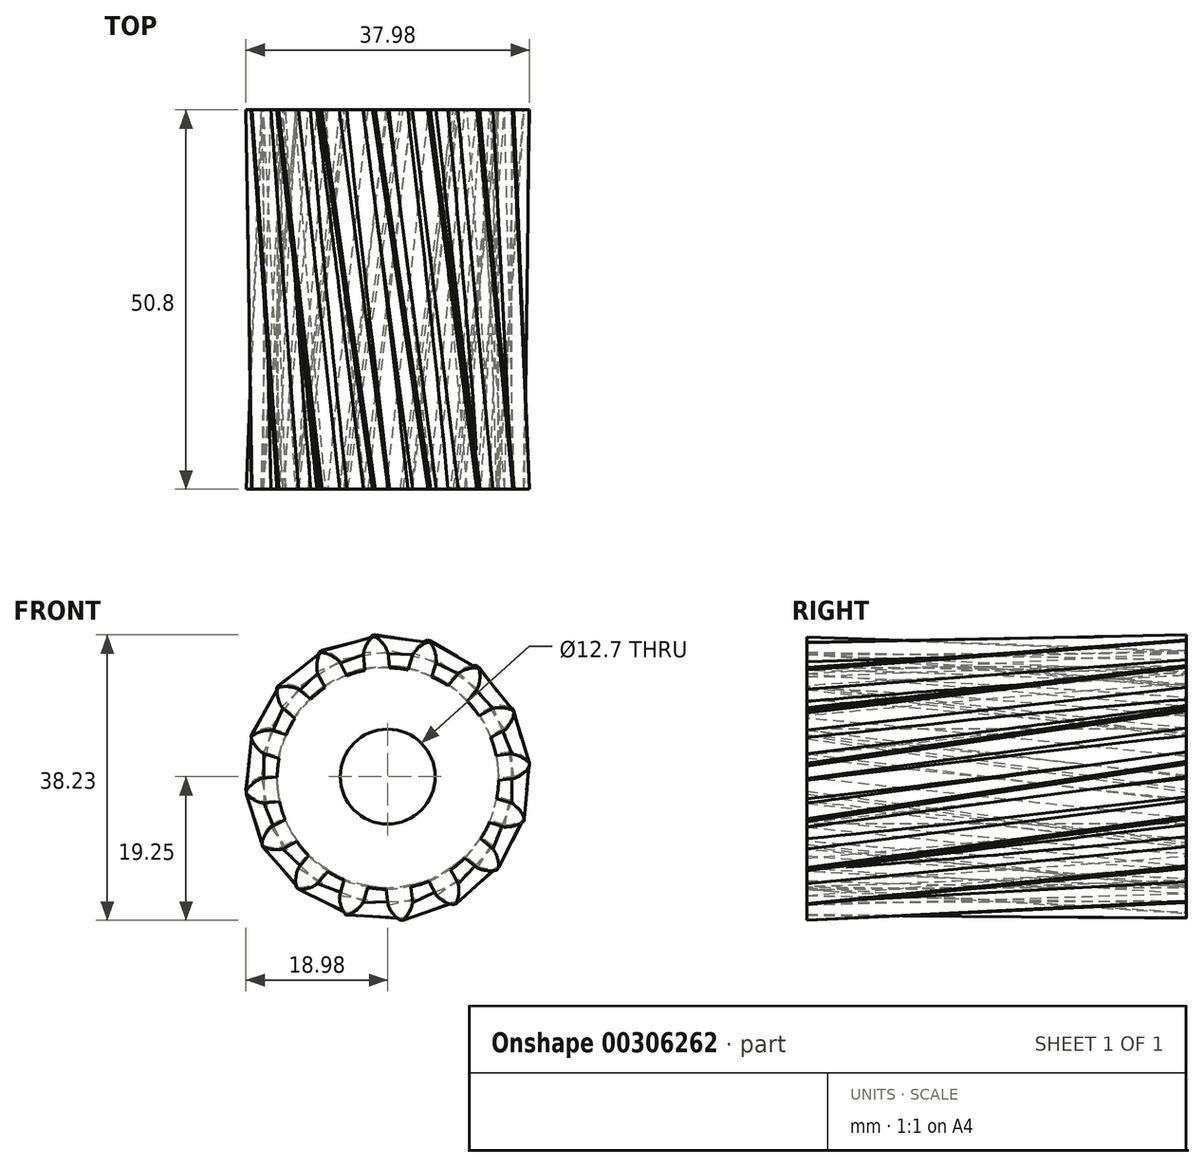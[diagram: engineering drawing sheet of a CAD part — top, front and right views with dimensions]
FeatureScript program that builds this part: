
annotation { "Feature Type Name" : "Feature", "Feature Type Description" : "" }
export const myFeature = defineFeature(function(context is Context, id is Id, definition is map)
    precondition{}
    {
        {
            var Q0;
            Q0=qCreatedBy(makeId("Front.planeOp"),FACE);
            var sketch = newSketch(context, id + "F0", { "sketchPlane" : qUnion([Q0])});
            skCircle(sketch, "E0", {"center": v(0, 0) * mm, "radius": 14.82 * mm});
            skArc(sketch, "E1.trimOffspring", {"start": v(0, 16.93) * mm, "mid": v(-0.67, 18.09) * mm, "end": v(-1.67, 18.98) * mm});
            skLineSegment(sketch, "E2", {"start": v(0, 16.93) * mm, "end": v(0.2, 14.82) * mm});
            skLineSegment(sketch, "E3", {"start": v(-1.67, 18.98) * mm, "end": v(-1.87, 18.96) * mm});
            skLineSegment(sketch, "E4.MirrorCS", {"start": v(-2.06, 18.94) * mm, "end": v(-1.87, 18.96) * mm});
            skArc(sketch, "E5.MirrorCS", {"start": v(-3.3, 16.6) * mm, "mid": v(-2.87, 17.87) * mm, "end": v(-2.06, 18.94) * mm});
            skLineSegment(sketch, "E6.MirrorCS", {"start": v(-3.3, 16.6) * mm, "end": v(-3.1, 14.5) * mm});
            skPoint(sketch, "E7.orphan", {"position": v(-2.98, 13.34) * mm});
            skPoint(sketch, "E8.orphan", {"position": v(0.32, 13.66) * mm});
            skLineSegment(sketch, "E9.1.0", {"start": v(-9.4, 14.08) * mm, "end": v(-8.4, 12.2) * mm});
            skArc(sketch, "E9.1.1", {"start": v(-9.4, 14.08) * mm, "mid": v(-9.49, 15.41) * mm, "end": v(-9.15, 16.7) * mm});
            skLineSegment(sketch, "E9.1.2", {"start": v(-8.8, 16.9) * mm, "end": v(-8.98, 16.8) * mm});
            skLineSegment(sketch, "E9.1.3", {"start": v(-9.15, 16.7) * mm, "end": v(-8.98, 16.8) * mm});
            skArc(sketch, "E9.1.4", {"start": v(-6.48, 15.64) * mm, "mid": v(-7.54, 16.45) * mm, "end": v(-8.8, 16.9) * mm});
            skLineSegment(sketch, "E9.1.5", {"start": v(-6.48, 15.64) * mm, "end": v(-5.48, 13.77) * mm});
            skLineSegment(sketch, "E9.2.0", {"start": v(-14.08, 9.4) * mm, "end": v(-12.44, 8.06) * mm});
            skArc(sketch, "E9.2.1", {"start": v(-14.08, 9.4) * mm, "mid": v(-14.67, 10.6) * mm, "end": v(-14.85, 11.93) * mm});
            skLineSegment(sketch, "E9.2.2", {"start": v(-14.6, 12.24) * mm, "end": v(-14.73, 12.09) * mm});
            skLineSegment(sketch, "E9.2.3", {"start": v(-14.85, 11.93) * mm, "end": v(-14.73, 12.09) * mm});
            skArc(sketch, "E9.2.4", {"start": v(-11.97, 11.97) * mm, "mid": v(-13.26, 12.31) * mm, "end": v(-14.6, 12.24) * mm});
            skLineSegment(sketch, "E9.2.5", {"start": v(-11.97, 11.97) * mm, "end": v(-10.33, 10.63) * mm});
            skLineSegment(sketch, "E9.3.0", {"start": v(-16.6, 3.3) * mm, "end": v(-14.58, 2.69) * mm});
            skArc(sketch, "E9.3.1", {"start": v(-16.6, 3.3) * mm, "mid": v(-17.6, 4.19) * mm, "end": v(-18.29, 5.34) * mm});
            skLineSegment(sketch, "E9.3.2", {"start": v(-18.17, 5.72) * mm, "end": v(-18.23, 5.53) * mm});
            skLineSegment(sketch, "E9.3.3", {"start": v(-18.29, 5.34) * mm, "end": v(-18.23, 5.53) * mm});
            skArc(sketch, "E9.3.4", {"start": v(-15.64, 6.48) * mm, "mid": v(-16.97, 6.3) * mm, "end": v(-18.17, 5.72) * mm});
            skLineSegment(sketch, "E9.3.5", {"start": v(-15.64, 6.48) * mm, "end": v(-13.61, 5.86) * mm});
            skLineSegment(sketch, "E9.4.0", {"start": v(-16.6, -3.3) * mm, "end": v(-14.5, -3.1) * mm});
            skArc(sketch, "E9.4.1", {"start": v(-16.6, -3.3) * mm, "mid": v(-17.87, -2.87) * mm, "end": v(-18.94, -2.06) * mm});
            skLineSegment(sketch, "E9.4.2", {"start": v(-18.98, -1.67) * mm, "end": v(-18.96, -1.87) * mm});
            skLineSegment(sketch, "E9.4.3", {"start": v(-18.94, -2.06) * mm, "end": v(-18.96, -1.87) * mm});
            skArc(sketch, "E9.4.4", {"start": v(-16.93, 0) * mm, "mid": v(-18.09, -0.67) * mm, "end": v(-18.98, -1.67) * mm});
            skLineSegment(sketch, "E9.4.5", {"start": v(-16.93, 0) * mm, "end": v(-14.82, 0.2) * mm});
            skLineSegment(sketch, "E9.5.0", {"start": v(-14.08, -9.4) * mm, "end": v(-12.2, -8.4) * mm});
            skArc(sketch, "E9.5.1", {"start": v(-14.08, -9.4) * mm, "mid": v(-15.41, -9.49) * mm, "end": v(-16.7, -9.15) * mm});
            skLineSegment(sketch, "E9.5.2", {"start": v(-16.9, -8.8) * mm, "end": v(-16.8, -8.98) * mm});
            skLineSegment(sketch, "E9.5.3", {"start": v(-16.7, -9.15) * mm, "end": v(-16.8, -8.98) * mm});
            skArc(sketch, "E9.5.4", {"start": v(-15.64, -6.48) * mm, "mid": v(-16.45, -7.54) * mm, "end": v(-16.9, -8.8) * mm});
            skLineSegment(sketch, "E9.5.5", {"start": v(-15.64, -6.48) * mm, "end": v(-13.77, -5.48) * mm});
            skLineSegment(sketch, "E9.6.0", {"start": v(-9.4, -14.08) * mm, "end": v(-8.06, -12.44) * mm});
            skArc(sketch, "E9.6.1", {"start": v(-9.4, -14.08) * mm, "mid": v(-10.6, -14.67) * mm, "end": v(-11.93, -14.85) * mm});
            skLineSegment(sketch, "E9.6.2", {"start": v(-12.24, -14.6) * mm, "end": v(-12.09, -14.73) * mm});
            skLineSegment(sketch, "E9.6.3", {"start": v(-11.93, -14.85) * mm, "end": v(-12.09, -14.73) * mm});
            skArc(sketch, "E9.6.4", {"start": v(-11.97, -11.97) * mm, "mid": v(-12.31, -13.26) * mm, "end": v(-12.24, -14.6) * mm});
            skLineSegment(sketch, "E9.6.5", {"start": v(-11.97, -11.97) * mm, "end": v(-10.63, -10.33) * mm});
            skLineSegment(sketch, "E9.7.0", {"start": v(-3.3, -16.6) * mm, "end": v(-2.69, -14.58) * mm});
            skArc(sketch, "E9.7.1", {"start": v(-3.3, -16.6) * mm, "mid": v(-4.19, -17.6) * mm, "end": v(-5.34, -18.29) * mm});
            skLineSegment(sketch, "E9.7.2", {"start": v(-5.72, -18.17) * mm, "end": v(-5.53, -18.23) * mm});
            skLineSegment(sketch, "E9.7.3", {"start": v(-5.34, -18.29) * mm, "end": v(-5.53, -18.23) * mm});
            skArc(sketch, "E9.7.4", {"start": v(-6.48, -15.64) * mm, "mid": v(-6.3, -16.97) * mm, "end": v(-5.72, -18.17) * mm});
            skLineSegment(sketch, "E9.7.5", {"start": v(-6.48, -15.64) * mm, "end": v(-5.86, -13.61) * mm});
            skLineSegment(sketch, "E9.8.0", {"start": v(3.3, -16.6) * mm, "end": v(3.1, -14.5) * mm});
            skArc(sketch, "E9.8.1", {"start": v(3.3, -16.6) * mm, "mid": v(2.87, -17.87) * mm, "end": v(2.06, -18.94) * mm});
            skLineSegment(sketch, "E9.8.2", {"start": v(1.67, -18.98) * mm, "end": v(1.87, -18.96) * mm});
            skLineSegment(sketch, "E9.8.3", {"start": v(2.06, -18.94) * mm, "end": v(1.87, -18.96) * mm});
            skArc(sketch, "E9.8.4", {"start": v(0, -16.93) * mm, "mid": v(0.67, -18.09) * mm, "end": v(1.67, -18.98) * mm});
            skLineSegment(sketch, "E9.8.5", {"start": v(0, -16.93) * mm, "end": v(-0.2, -14.82) * mm});
            skLineSegment(sketch, "E9.9.0", {"start": v(9.4, -14.08) * mm, "end": v(8.4, -12.2) * mm});
            skArc(sketch, "E9.9.1", {"start": v(9.4, -14.08) * mm, "mid": v(9.49, -15.41) * mm, "end": v(9.15, -16.7) * mm});
            skLineSegment(sketch, "E9.9.2", {"start": v(8.8, -16.9) * mm, "end": v(8.98, -16.8) * mm});
            skLineSegment(sketch, "E9.9.3", {"start": v(9.15, -16.7) * mm, "end": v(8.98, -16.8) * mm});
            skArc(sketch, "E9.9.4", {"start": v(6.48, -15.64) * mm, "mid": v(7.54, -16.45) * mm, "end": v(8.8, -16.9) * mm});
            skLineSegment(sketch, "E9.9.5", {"start": v(6.48, -15.64) * mm, "end": v(5.48, -13.77) * mm});
            skLineSegment(sketch, "E9.10.0", {"start": v(14.08, -9.4) * mm, "end": v(12.44, -8.06) * mm});
            skArc(sketch, "E9.10.1", {"start": v(14.08, -9.4) * mm, "mid": v(14.67, -10.6) * mm, "end": v(14.85, -11.93) * mm});
            skLineSegment(sketch, "E9.10.2", {"start": v(14.6, -12.24) * mm, "end": v(14.73, -12.09) * mm});
            skLineSegment(sketch, "E9.10.3", {"start": v(14.85, -11.93) * mm, "end": v(14.73, -12.09) * mm});
            skArc(sketch, "E9.10.4", {"start": v(11.97, -11.97) * mm, "mid": v(13.26, -12.31) * mm, "end": v(14.6, -12.24) * mm});
            skLineSegment(sketch, "E9.10.5", {"start": v(11.97, -11.97) * mm, "end": v(10.33, -10.63) * mm});
            skLineSegment(sketch, "E9.11.0", {"start": v(16.6, -3.3) * mm, "end": v(14.58, -2.69) * mm});
            skArc(sketch, "E9.11.1", {"start": v(16.6, -3.3) * mm, "mid": v(17.6, -4.19) * mm, "end": v(18.29, -5.34) * mm});
            skLineSegment(sketch, "E9.11.2", {"start": v(18.17, -5.72) * mm, "end": v(18.23, -5.53) * mm});
            skLineSegment(sketch, "E9.11.3", {"start": v(18.29, -5.34) * mm, "end": v(18.23, -5.53) * mm});
            skArc(sketch, "E9.11.4", {"start": v(15.64, -6.48) * mm, "mid": v(16.97, -6.3) * mm, "end": v(18.17, -5.72) * mm});
            skLineSegment(sketch, "E9.11.5", {"start": v(15.64, -6.48) * mm, "end": v(13.61, -5.86) * mm});
            skLineSegment(sketch, "E9.12.0", {"start": v(16.6, 3.3) * mm, "end": v(14.5, 3.1) * mm});
            skArc(sketch, "E9.12.1", {"start": v(16.6, 3.3) * mm, "mid": v(17.87, 2.87) * mm, "end": v(18.94, 2.06) * mm});
            skLineSegment(sketch, "E9.12.2", {"start": v(18.98, 1.67) * mm, "end": v(18.96, 1.87) * mm});
            skLineSegment(sketch, "E9.12.3", {"start": v(18.94, 2.06) * mm, "end": v(18.96, 1.87) * mm});
            skArc(sketch, "E9.12.4", {"start": v(16.93, 0) * mm, "mid": v(18.09, 0.67) * mm, "end": v(18.98, 1.67) * mm});
            skLineSegment(sketch, "E9.12.5", {"start": v(16.93, 0) * mm, "end": v(14.82, -0.2) * mm});
            skLineSegment(sketch, "E9.13.0", {"start": v(14.08, 9.4) * mm, "end": v(12.2, 8.4) * mm});
            skArc(sketch, "E9.13.1", {"start": v(14.08, 9.4) * mm, "mid": v(15.41, 9.49) * mm, "end": v(16.7, 9.15) * mm});
            skLineSegment(sketch, "E9.13.2", {"start": v(16.9, 8.8) * mm, "end": v(16.8, 8.98) * mm});
            skLineSegment(sketch, "E9.13.3", {"start": v(16.7, 9.15) * mm, "end": v(16.8, 8.98) * mm});
            skArc(sketch, "E9.13.4", {"start": v(15.64, 6.48) * mm, "mid": v(16.45, 7.54) * mm, "end": v(16.9, 8.8) * mm});
            skLineSegment(sketch, "E9.13.5", {"start": v(15.64, 6.48) * mm, "end": v(13.77, 5.48) * mm});
            skLineSegment(sketch, "E9.14.0", {"start": v(9.4, 14.08) * mm, "end": v(8.06, 12.44) * mm});
            skArc(sketch, "E9.14.1", {"start": v(9.4, 14.08) * mm, "mid": v(10.6, 14.67) * mm, "end": v(11.93, 14.85) * mm});
            skLineSegment(sketch, "E9.14.2", {"start": v(12.24, 14.6) * mm, "end": v(12.09, 14.73) * mm});
            skLineSegment(sketch, "E9.14.3", {"start": v(11.93, 14.85) * mm, "end": v(12.09, 14.73) * mm});
            skArc(sketch, "E9.14.4", {"start": v(11.97, 11.97) * mm, "mid": v(12.31, 13.26) * mm, "end": v(12.24, 14.6) * mm});
            skLineSegment(sketch, "E9.14.5", {"start": v(11.97, 11.97) * mm, "end": v(10.63, 10.33) * mm});
            skLineSegment(sketch, "E9.15.0", {"start": v(3.3, 16.6) * mm, "end": v(2.69, 14.58) * mm});
            skArc(sketch, "E9.15.1", {"start": v(3.3, 16.6) * mm, "mid": v(4.19, 17.6) * mm, "end": v(5.34, 18.29) * mm});
            skLineSegment(sketch, "E9.15.2", {"start": v(5.72, 18.17) * mm, "end": v(5.53, 18.23) * mm});
            skLineSegment(sketch, "E9.15.3", {"start": v(5.34, 18.29) * mm, "end": v(5.53, 18.23) * mm});
            skArc(sketch, "E9.15.4", {"start": v(6.48, 15.64) * mm, "mid": v(6.3, 16.97) * mm, "end": v(5.72, 18.17) * mm});
            skLineSegment(sketch, "E9.15.5", {"start": v(6.48, 15.64) * mm, "end": v(5.86, 13.61) * mm});
            skSolve(sketch);
        }
        {
            var Q0;
            Q0=qCreatedBy(makeId("Front.planeOp"),FACE);
            cPlane(context, id + "F1", {"entities" : qUnion([Q0]), "cplaneType" : CPlaneType.OFFSET, "offset" : 50.8 * mm, "width" : 152.4 * mm, "height" : 152.4 * mm});
        }
        {
            var Q0;
            Q0=qCreatedBy(id+"F1.planeOp",FACE);
            var sketch = newSketch(context, id + "F2", { "sketchPlane" : qUnion([Q0])});
            skCircle(sketch, "E10", {"center": v(0.03, -0.27) * mm, "radius": 14.82 * mm});
            skArc(sketch, "E11.trimOffspring", {"start": v(0.03, 16.66) * mm, "mid": v(-0.65, 17.82) * mm, "end": v(-1.65, 18.7) * mm});
            skLineSegment(sketch, "E12", {"start": v(0.03, 16.66) * mm, "end": v(0.23, 14.55) * mm});
            skLineSegment(sketch, "E13", {"start": v(-1.65, 18.7) * mm, "end": v(-1.84, 18.69) * mm});
            skLineSegment(sketch, "E14.MirrorCS", {"start": v(-2.03, 18.67) * mm, "end": v(-1.84, 18.69) * mm});
            skArc(sketch, "E15.MirrorCS", {"start": v(-3.28, 16.33) * mm, "mid": v(-2.84, 17.6) * mm, "end": v(-2.03, 18.67) * mm});
            skLineSegment(sketch, "E16.MirrorCS", {"start": v(-3.28, 16.33) * mm, "end": v(-3.07, 14.22) * mm});
            skPoint(sketch, "E17.orphan", {"position": v(-2.95, 13.07) * mm});
            skPoint(sketch, "E18.orphan", {"position": v(0.35, 13.4) * mm});
            skLineSegment(sketch, "E19.1.0", {"start": v(-9.38, 13.8) * mm, "end": v(-8.38, 11.94) * mm});
            skArc(sketch, "E19.1.1", {"start": v(-9.38, 13.8) * mm, "mid": v(-9.46, 15.14) * mm, "end": v(-9.12, 16.44) * mm});
            skLineSegment(sketch, "E19.1.2", {"start": v(-8.78, 16.62) * mm, "end": v(-8.95, 16.53) * mm});
            skLineSegment(sketch, "E19.1.3", {"start": v(-9.12, 16.44) * mm, "end": v(-8.95, 16.53) * mm});
            skArc(sketch, "E19.1.4", {"start": v(-6.45, 15.37) * mm, "mid": v(-7.52, 16.18) * mm, "end": v(-8.78, 16.62) * mm});
            skLineSegment(sketch, "E19.1.5", {"start": v(-6.45, 15.37) * mm, "end": v(-5.45, 13.5) * mm});
            skLineSegment(sketch, "E19.2.0", {"start": v(-14.05, 9.14) * mm, "end": v(-12.41, 7.8) * mm});
            skArc(sketch, "E19.2.1", {"start": v(-14.05, 9.14) * mm, "mid": v(-14.64, 10.34) * mm, "end": v(-14.82, 11.66) * mm});
            skLineSegment(sketch, "E19.2.2", {"start": v(-14.57, 11.97) * mm, "end": v(-14.7, 11.82) * mm});
            skLineSegment(sketch, "E19.2.3", {"start": v(-14.82, 11.66) * mm, "end": v(-14.7, 11.82) * mm});
            skArc(sketch, "E19.2.4", {"start": v(-11.94, 11.7) * mm, "mid": v(-13.24, 12.04) * mm, "end": v(-14.57, 11.97) * mm});
            skLineSegment(sketch, "E19.2.5", {"start": v(-11.94, 11.7) * mm, "end": v(-10.3, 10.36) * mm});
            skLineSegment(sketch, "E19.3.0", {"start": v(-16.58, 3.03) * mm, "end": v(-14.55, 2.42) * mm});
            skArc(sketch, "E19.3.1", {"start": v(-16.58, 3.03) * mm, "mid": v(-17.58, 3.92) * mm, "end": v(-18.26, 5.07) * mm});
            skLineSegment(sketch, "E19.3.2", {"start": v(-18.15, 5.45) * mm, "end": v(-18.2, 5.26) * mm});
            skLineSegment(sketch, "E19.3.3", {"start": v(-18.26, 5.07) * mm, "end": v(-18.2, 5.26) * mm});
            skArc(sketch, "E19.3.4", {"start": v(-15.61, 6.2) * mm, "mid": v(-16.94, 6.03) * mm, "end": v(-18.15, 5.45) * mm});
            skLineSegment(sketch, "E19.3.5", {"start": v(-15.61, 6.2) * mm, "end": v(-13.59, 5.6) * mm});
            skLineSegment(sketch, "E19.4.0", {"start": v(-16.58, -3.57) * mm, "end": v(-14.47, -3.36) * mm});
            skArc(sketch, "E19.4.1", {"start": v(-16.58, -3.57) * mm, "mid": v(-17.84, -3.14) * mm, "end": v(-18.91, -2.33) * mm});
            skLineSegment(sketch, "E19.4.2", {"start": v(-18.95, -1.94) * mm, "end": v(-18.93, -2.14) * mm});
            skLineSegment(sketch, "E19.4.3", {"start": v(-18.91, -2.33) * mm, "end": v(-18.93, -2.14) * mm});
            skArc(sketch, "E19.4.4", {"start": v(-16.9, -0.27) * mm, "mid": v(-18.06, -0.94) * mm, "end": v(-18.95, -1.94) * mm});
            skLineSegment(sketch, "E19.4.5", {"start": v(-16.9, -0.27) * mm, "end": v(-14.8, -0.06) * mm});
            skLineSegment(sketch, "E19.5.0", {"start": v(-14.05, -9.68) * mm, "end": v(-12.18, -8.68) * mm});
            skArc(sketch, "E19.5.1", {"start": v(-14.05, -9.68) * mm, "mid": v(-15.39, -9.76) * mm, "end": v(-16.68, -9.42) * mm});
            skLineSegment(sketch, "E19.5.2", {"start": v(-16.87, -9.08) * mm, "end": v(-16.77, -9.25) * mm});
            skLineSegment(sketch, "E19.5.3", {"start": v(-16.68, -9.42) * mm, "end": v(-16.77, -9.25) * mm});
            skArc(sketch, "E19.5.4", {"start": v(-15.61, -6.75) * mm, "mid": v(-16.43, -7.81) * mm, "end": v(-16.87, -9.08) * mm});
            skLineSegment(sketch, "E19.5.5", {"start": v(-15.61, -6.75) * mm, "end": v(-13.74, -5.75) * mm});
            skLineSegment(sketch, "E19.6.0", {"start": v(-9.38, -14.35) * mm, "end": v(-8.03, -12.7) * mm});
            skArc(sketch, "E19.6.1", {"start": v(-9.38, -14.35) * mm, "mid": v(-10.58, -14.94) * mm, "end": v(-11.9, -15.12) * mm});
            skLineSegment(sketch, "E19.6.2", {"start": v(-12.2, -14.87) * mm, "end": v(-12.06, -15) * mm});
            skLineSegment(sketch, "E19.6.3", {"start": v(-11.9, -15.12) * mm, "end": v(-12.06, -15) * mm});
            skArc(sketch, "E19.6.4", {"start": v(-11.94, -12.24) * mm, "mid": v(-12.29, -13.53) * mm, "end": v(-12.2, -14.87) * mm});
            skLineSegment(sketch, "E19.6.5", {"start": v(-11.94, -12.24) * mm, "end": v(-10.6, -10.6) * mm});
            skLineSegment(sketch, "E19.7.0", {"start": v(-3.28, -16.87) * mm, "end": v(-2.66, -14.85) * mm});
            skArc(sketch, "E19.7.1", {"start": v(-3.28, -16.87) * mm, "mid": v(-4.16, -17.88) * mm, "end": v(-5.32, -18.56) * mm});
            skLineSegment(sketch, "E19.7.2", {"start": v(-5.69, -18.44) * mm, "end": v(-5.5, -18.5) * mm});
            skLineSegment(sketch, "E19.7.3", {"start": v(-5.32, -18.56) * mm, "end": v(-5.5, -18.5) * mm});
            skArc(sketch, "E19.7.4", {"start": v(-6.45, -15.91) * mm, "mid": v(-6.27, -17.24) * mm, "end": v(-5.69, -18.44) * mm});
            skLineSegment(sketch, "E19.7.5", {"start": v(-6.45, -15.91) * mm, "end": v(-5.84, -13.88) * mm});
            skLineSegment(sketch, "E19.8.0", {"start": v(3.33, -16.87) * mm, "end": v(3.12, -14.76) * mm});
            skArc(sketch, "E19.8.1", {"start": v(3.33, -16.87) * mm, "mid": v(2.9, -18.14) * mm, "end": v(2.09, -19.2) * mm});
            skLineSegment(sketch, "E19.8.2", {"start": v(1.7, -19.25) * mm, "end": v(1.9, -19.23) * mm});
            skLineSegment(sketch, "E19.8.3", {"start": v(2.09, -19.2) * mm, "end": v(1.9, -19.23) * mm});
            skArc(sketch, "E19.8.4", {"start": v(0.03, -17.2) * mm, "mid": v(0.7, -18.36) * mm, "end": v(1.7, -19.25) * mm});
            skLineSegment(sketch, "E19.8.5", {"start": v(0.03, -17.2) * mm, "end": v(-0.18, -15.09) * mm});
            skLineSegment(sketch, "E19.9.0", {"start": v(9.43, -14.35) * mm, "end": v(8.43, -12.48) * mm});
            skArc(sketch, "E19.9.1", {"start": v(9.43, -14.35) * mm, "mid": v(9.52, -15.68) * mm, "end": v(9.18, -16.98) * mm});
            skLineSegment(sketch, "E19.9.2", {"start": v(8.83, -17.16) * mm, "end": v(9, -17.07) * mm});
            skLineSegment(sketch, "E19.9.3", {"start": v(9.18, -16.98) * mm, "end": v(9, -17.07) * mm});
            skArc(sketch, "E19.9.4", {"start": v(6.5, -15.91) * mm, "mid": v(7.57, -16.72) * mm, "end": v(8.83, -17.16) * mm});
            skLineSegment(sketch, "E19.9.5", {"start": v(6.5, -15.91) * mm, "end": v(5.5, -14.04) * mm});
            skLineSegment(sketch, "E19.10.0", {"start": v(14.1, -9.68) * mm, "end": v(12.46, -8.33) * mm});
            skArc(sketch, "E19.10.1", {"start": v(14.1, -9.68) * mm, "mid": v(14.7, -10.88) * mm, "end": v(14.88, -12.2) * mm});
            skLineSegment(sketch, "E19.10.2", {"start": v(14.63, -12.5) * mm, "end": v(14.75, -12.36) * mm});
            skLineSegment(sketch, "E19.10.3", {"start": v(14.88, -12.2) * mm, "end": v(14.75, -12.36) * mm});
            skArc(sketch, "E19.10.4", {"start": v(12, -12.24) * mm, "mid": v(13.3, -12.58) * mm, "end": v(14.63, -12.5) * mm});
            skLineSegment(sketch, "E19.10.5", {"start": v(12, -12.24) * mm, "end": v(10.36, -10.9) * mm});
            skLineSegment(sketch, "E19.11.0", {"start": v(16.63, -3.57) * mm, "end": v(14.6, -2.96) * mm});
            skArc(sketch, "E19.11.1", {"start": v(16.63, -3.57) * mm, "mid": v(17.63, -4.46) * mm, "end": v(18.31, -5.61) * mm});
            skLineSegment(sketch, "E19.11.2", {"start": v(18.2, -5.99) * mm, "end": v(18.26, -5.8) * mm});
            skLineSegment(sketch, "E19.11.3", {"start": v(18.31, -5.61) * mm, "end": v(18.26, -5.8) * mm});
            skArc(sketch, "E19.11.4", {"start": v(15.67, -6.75) * mm, "mid": v(17, -6.57) * mm, "end": v(18.2, -5.99) * mm});
            skLineSegment(sketch, "E19.11.5", {"start": v(15.67, -6.75) * mm, "end": v(13.64, -6.13) * mm});
            skLineSegment(sketch, "E19.12.0", {"start": v(16.63, 3.03) * mm, "end": v(14.52, 2.82) * mm});
            skArc(sketch, "E19.12.1", {"start": v(16.63, 3.03) * mm, "mid": v(17.9, 2.6) * mm, "end": v(18.96, 1.8) * mm});
            skLineSegment(sketch, "E19.12.2", {"start": v(19, 1.4) * mm, "end": v(18.99, 1.6) * mm});
            skLineSegment(sketch, "E19.12.3", {"start": v(18.96, 1.8) * mm, "end": v(18.99, 1.6) * mm});
            skArc(sketch, "E19.12.4", {"start": v(16.96, -0.27) * mm, "mid": v(18.11, 0.4) * mm, "end": v(19, 1.4) * mm});
            skLineSegment(sketch, "E19.12.5", {"start": v(16.96, -0.27) * mm, "end": v(14.85, -0.48) * mm});
            skLineSegment(sketch, "E19.13.0", {"start": v(14.1, 9.14) * mm, "end": v(12.23, 8.14) * mm});
            skArc(sketch, "E19.13.1", {"start": v(14.1, 9.14) * mm, "mid": v(15.44, 9.22) * mm, "end": v(16.73, 8.88) * mm});
            skLineSegment(sketch, "E19.13.2", {"start": v(16.92, 8.54) * mm, "end": v(16.83, 8.71) * mm});
            skLineSegment(sketch, "E19.13.3", {"start": v(16.73, 8.88) * mm, "end": v(16.83, 8.71) * mm});
            skArc(sketch, "E19.13.4", {"start": v(15.67, 6.2) * mm, "mid": v(16.48, 7.27) * mm, "end": v(16.92, 8.54) * mm});
            skLineSegment(sketch, "E19.13.5", {"start": v(15.67, 6.2) * mm, "end": v(13.8, 5.2) * mm});
            skLineSegment(sketch, "E19.14.0", {"start": v(9.43, 13.8) * mm, "end": v(8.09, 12.17) * mm});
            skArc(sketch, "E19.14.1", {"start": v(9.43, 13.8) * mm, "mid": v(10.63, 14.4) * mm, "end": v(11.96, 14.58) * mm});
            skLineSegment(sketch, "E19.14.2", {"start": v(12.26, 14.33) * mm, "end": v(12.11, 14.46) * mm});
            skLineSegment(sketch, "E19.14.3", {"start": v(11.96, 14.58) * mm, "end": v(12.11, 14.46) * mm});
            skArc(sketch, "E19.14.4", {"start": v(12, 11.7) * mm, "mid": v(12.34, 13) * mm, "end": v(12.26, 14.33) * mm});
            skLineSegment(sketch, "E19.14.5", {"start": v(12, 11.7) * mm, "end": v(10.65, 10.06) * mm});
            skLineSegment(sketch, "E19.15.0", {"start": v(3.33, 16.33) * mm, "end": v(2.71, 14.3) * mm});
            skArc(sketch, "E19.15.1", {"start": v(3.33, 16.33) * mm, "mid": v(4.21, 17.34) * mm, "end": v(5.37, 18.02) * mm});
            skLineSegment(sketch, "E19.15.2", {"start": v(5.74, 17.9) * mm, "end": v(5.56, 17.96) * mm});
            skLineSegment(sketch, "E19.15.3", {"start": v(5.37, 18.02) * mm, "end": v(5.56, 17.96) * mm});
            skArc(sketch, "E19.15.4", {"start": v(6.5, 15.37) * mm, "mid": v(6.33, 16.7) * mm, "end": v(5.74, 17.9) * mm});
            skLineSegment(sketch, "E19.15.5", {"start": v(6.5, 15.37) * mm, "end": v(5.89, 13.34) * mm});
            skSolve(sketch);
        }
        {
            var Q0;
            {var subQ0=sQuery(id+"F0.wireOp",EDGE,"E0");var subQ18=makeQuery(id+"F0.imprint","INTERSECT",VERTEX,{"derivedFrom":[subQ0,sQuery(id+"F0.wireOp",EDGE,"E9.12.0")]});Q0=makeQuery(id+"F0.imprint","IMPRINT",FACE,{"disambiguationData":[TD([[makeQuery(id+"F0.imprint","IMPRINT",EDGE,{"disambiguationData":[TD([[subQ18,-1.0]])],"derivedFrom":subQ0}),1.0]])]});}
            var Q1;
            {var subQ0=sQuery(id+"F2.wireOp",EDGE,"E10");var subQ18=makeQuery(id+"F2.imprint","INTERSECT",VERTEX,{"derivedFrom":[subQ0,sQuery(id+"F2.wireOp",EDGE,"E19.12.0")]});Q1=makeQuery(id+"F2.imprint","IMPRINT",FACE,{"disambiguationData":[TD([[makeQuery(id+"F2.imprint","IMPRINT",EDGE,{"disambiguationData":[TD([[subQ18,-1.0]])],"derivedFrom":subQ0}),1.0]])]});}
            loft(context, id + "F3", {"sheetProfilesArray" : [{ "sheetProfileEntities" : qUnion([Q0]) }, { "sheetProfileEntities" : qUnion([Q1]) }]});
        }
        {
            var Q1;
            Q1=makeQuery(id+"F2.imprint","IMPRINT",FACE,{"disambiguationData":[TD([[makeQuery(id+"F2.imprint","IMPRINT",EDGE,{"derivedFrom":sQuery(id+"F2.wireOp",EDGE,"E11.trimOffspring")}),1.0]])]});
            var Q2;
            {var subQ0=sQuery(id+"F0.wireOp",EDGE,"E9.1.0");Q2=makeQuery(id+"F0.imprint","IMPRINT",FACE,{"disambiguationData":[TD([[makeQuery(id+"F0.imprint","IMPRINT",EDGE,{"derivedFrom":subQ0}),1.0]])]});}
            loft(context, id + "F4", {"operationType" : NewBodyOperationType.ADD, "sheetProfilesArray" : [{ "sheetProfileEntities" : qUnion([Q1]) }, { "sheetProfileEntities" : qUnion([Q2]) }]});
        }
        {
            var Q1;
            {var subQ0=sQuery(id+"F2.wireOp",EDGE,"E19.1.0");Q1=makeQuery(id+"F2.imprint","IMPRINT",FACE,{"disambiguationData":[TD([[makeQuery(id+"F2.imprint","IMPRINT",EDGE,{"derivedFrom":subQ0}),1.0]])]});}
            var Q2;
            {var subQ0=sQuery(id+"F0.wireOp",EDGE,"E9.2.0");Q2=makeQuery(id+"F0.imprint","IMPRINT",FACE,{"disambiguationData":[TD([[makeQuery(id+"F0.imprint","IMPRINT",EDGE,{"derivedFrom":subQ0}),1.0]])]});}
            loft(context, id + "F5", {"operationType" : NewBodyOperationType.ADD, "sheetProfilesArray" : [{ "sheetProfileEntities" : qUnion([Q1]) }, { "sheetProfileEntities" : qUnion([Q2]) }]});
        }
        {
            var Q1;
            {var subQ0=sQuery(id+"F2.wireOp",EDGE,"E19.2.0");Q1=makeQuery(id+"F2.imprint","IMPRINT",FACE,{"disambiguationData":[TD([[makeQuery(id+"F2.imprint","IMPRINT",EDGE,{"derivedFrom":subQ0}),1.0]])]});}
            var Q2;
            {var subQ0=sQuery(id+"F0.wireOp",EDGE,"E9.3.0");Q2=makeQuery(id+"F0.imprint","IMPRINT",FACE,{"disambiguationData":[TD([[makeQuery(id+"F0.imprint","IMPRINT",EDGE,{"derivedFrom":subQ0}),1.0]])]});}
            loft(context, id + "F6", {"operationType" : NewBodyOperationType.ADD, "sheetProfilesArray" : [{ "sheetProfileEntities" : qUnion([Q1]) }, { "sheetProfileEntities" : qUnion([Q2]) }]});
        }
        {
            var Q1;
            {var subQ0=sQuery(id+"F2.wireOp",EDGE,"E19.3.0");Q1=makeQuery(id+"F2.imprint","IMPRINT",FACE,{"disambiguationData":[TD([[makeQuery(id+"F2.imprint","IMPRINT",EDGE,{"derivedFrom":subQ0}),1.0]])]});}
            var Q2;
            {var subQ0=sQuery(id+"F0.wireOp",EDGE,"E9.4.0");Q2=makeQuery(id+"F0.imprint","IMPRINT",FACE,{"disambiguationData":[TD([[makeQuery(id+"F0.imprint","IMPRINT",EDGE,{"derivedFrom":subQ0}),1.0]])]});}
            loft(context, id + "F7", {"operationType" : NewBodyOperationType.ADD, "sheetProfilesArray" : [{ "sheetProfileEntities" : qUnion([Q1]) }, { "sheetProfileEntities" : qUnion([Q2]) }]});
        }
        {
            var Q1;
            {var subQ0=sQuery(id+"F2.wireOp",EDGE,"E19.4.0");Q1=makeQuery(id+"F2.imprint","IMPRINT",FACE,{"disambiguationData":[TD([[makeQuery(id+"F2.imprint","IMPRINT",EDGE,{"derivedFrom":subQ0}),1.0]])]});}
            var Q2;
            {var subQ0=sQuery(id+"F0.wireOp",EDGE,"E9.5.0");Q2=makeQuery(id+"F0.imprint","IMPRINT",FACE,{"disambiguationData":[TD([[makeQuery(id+"F0.imprint","IMPRINT",EDGE,{"derivedFrom":subQ0}),1.0]])]});}
            loft(context, id + "F8", {"operationType" : NewBodyOperationType.ADD, "sheetProfilesArray" : [{ "sheetProfileEntities" : qUnion([Q1]) }, { "sheetProfileEntities" : qUnion([Q2]) }]});
        }
        {
            var Q1;
            {var subQ0=sQuery(id+"F2.wireOp",EDGE,"E19.5.0");Q1=makeQuery(id+"F2.imprint","IMPRINT",FACE,{"disambiguationData":[TD([[makeQuery(id+"F2.imprint","IMPRINT",EDGE,{"derivedFrom":subQ0}),1.0]])]});}
            var Q2;
            {var subQ0=sQuery(id+"F0.wireOp",EDGE,"E9.6.0");Q2=makeQuery(id+"F0.imprint","IMPRINT",FACE,{"disambiguationData":[TD([[makeQuery(id+"F0.imprint","IMPRINT",EDGE,{"derivedFrom":subQ0}),1.0]])]});}
            loft(context, id + "F9", {"operationType" : NewBodyOperationType.ADD, "sheetProfilesArray" : [{ "sheetProfileEntities" : qUnion([Q1]) }, { "sheetProfileEntities" : qUnion([Q2]) }]});
        }
        {
            var Q1;
            {var subQ0=sQuery(id+"F2.wireOp",EDGE,"E19.6.0");Q1=makeQuery(id+"F2.imprint","IMPRINT",FACE,{"disambiguationData":[TD([[makeQuery(id+"F2.imprint","IMPRINT",EDGE,{"derivedFrom":subQ0}),1.0]])]});}
            var Q2;
            {var subQ0=sQuery(id+"F0.wireOp",EDGE,"E9.7.0");Q2=makeQuery(id+"F0.imprint","IMPRINT",FACE,{"disambiguationData":[TD([[makeQuery(id+"F0.imprint","IMPRINT",EDGE,{"derivedFrom":subQ0}),1.0]])]});}
            loft(context, id + "F10", {"operationType" : NewBodyOperationType.ADD, "sheetProfilesArray" : [{ "sheetProfileEntities" : qUnion([Q1]) }, { "sheetProfileEntities" : qUnion([Q2]) }]});
        }
        {
            var Q1;
            {var subQ0=sQuery(id+"F2.wireOp",EDGE,"E19.7.0");Q1=makeQuery(id+"F2.imprint","IMPRINT",FACE,{"disambiguationData":[TD([[makeQuery(id+"F2.imprint","IMPRINT",EDGE,{"derivedFrom":subQ0}),1.0]])]});}
            var Q2;
            {var subQ0=sQuery(id+"F0.wireOp",EDGE,"E9.8.0");Q2=makeQuery(id+"F0.imprint","IMPRINT",FACE,{"disambiguationData":[TD([[makeQuery(id+"F0.imprint","IMPRINT",EDGE,{"derivedFrom":subQ0}),1.0]])]});}
            loft(context, id + "F11", {"operationType" : NewBodyOperationType.ADD, "sheetProfilesArray" : [{ "sheetProfileEntities" : qUnion([Q1]) }, { "sheetProfileEntities" : qUnion([Q2]) }]});
        }
        {
            var Q1;
            {var subQ0=sQuery(id+"F2.wireOp",EDGE,"E19.8.0");Q1=makeQuery(id+"F2.imprint","IMPRINT",FACE,{"disambiguationData":[TD([[makeQuery(id+"F2.imprint","IMPRINT",EDGE,{"derivedFrom":subQ0}),1.0]])]});}
            var Q2;
            {var subQ0=sQuery(id+"F0.wireOp",EDGE,"E9.9.0");Q2=makeQuery(id+"F0.imprint","IMPRINT",FACE,{"disambiguationData":[TD([[makeQuery(id+"F0.imprint","IMPRINT",EDGE,{"derivedFrom":subQ0}),1.0]])]});}
            loft(context, id + "F12", {"operationType" : NewBodyOperationType.ADD, "sheetProfilesArray" : [{ "sheetProfileEntities" : qUnion([Q1]) }, { "sheetProfileEntities" : qUnion([Q2]) }]});
        }
        {
            var Q1;
            {var subQ0=sQuery(id+"F2.wireOp",EDGE,"E19.9.0");Q1=makeQuery(id+"F2.imprint","IMPRINT",FACE,{"disambiguationData":[TD([[makeQuery(id+"F2.imprint","IMPRINT",EDGE,{"derivedFrom":subQ0}),1.0]])]});}
            var Q2;
            {var subQ0=sQuery(id+"F0.wireOp",EDGE,"E9.10.0");Q2=makeQuery(id+"F0.imprint","IMPRINT",FACE,{"disambiguationData":[TD([[makeQuery(id+"F0.imprint","IMPRINT",EDGE,{"derivedFrom":subQ0}),1.0]])]});}
            loft(context, id + "F13", {"operationType" : NewBodyOperationType.ADD, "sheetProfilesArray" : [{ "sheetProfileEntities" : qUnion([Q1]) }, { "sheetProfileEntities" : qUnion([Q2]) }]});
        }
        {
            var Q1;
            {var subQ0=sQuery(id+"F2.wireOp",EDGE,"E19.10.0");Q1=makeQuery(id+"F2.imprint","IMPRINT",FACE,{"disambiguationData":[TD([[makeQuery(id+"F2.imprint","IMPRINT",EDGE,{"derivedFrom":subQ0}),1.0]])]});}
            var Q2;
            {var subQ0=sQuery(id+"F0.wireOp",EDGE,"E9.11.0");Q2=makeQuery(id+"F0.imprint","IMPRINT",FACE,{"disambiguationData":[TD([[makeQuery(id+"F0.imprint","IMPRINT",EDGE,{"derivedFrom":subQ0}),1.0]])]});}
            loft(context, id + "F14", {"operationType" : NewBodyOperationType.ADD, "sheetProfilesArray" : [{ "sheetProfileEntities" : qUnion([Q1]) }, { "sheetProfileEntities" : qUnion([Q2]) }]});
        }
        {
            var Q1;
            {var subQ0=sQuery(id+"F2.wireOp",EDGE,"E19.11.0");Q1=makeQuery(id+"F2.imprint","IMPRINT",FACE,{"disambiguationData":[TD([[makeQuery(id+"F2.imprint","IMPRINT",EDGE,{"derivedFrom":subQ0}),1.0]])]});}
            var Q2;
            {var subQ0=sQuery(id+"F0.wireOp",EDGE,"E9.12.0");Q2=makeQuery(id+"F0.imprint","IMPRINT",FACE,{"disambiguationData":[TD([[makeQuery(id+"F0.imprint","IMPRINT",EDGE,{"derivedFrom":subQ0}),1.0]])]});}
            loft(context, id + "F15", {"operationType" : NewBodyOperationType.ADD, "sheetProfilesArray" : [{ "sheetProfileEntities" : qUnion([Q1]) }, { "sheetProfileEntities" : qUnion([Q2]) }]});
        }
        {
            var Q1;
            {var subQ0=sQuery(id+"F2.wireOp",EDGE,"E19.12.0");Q1=makeQuery(id+"F2.imprint","IMPRINT",FACE,{"disambiguationData":[TD([[makeQuery(id+"F2.imprint","IMPRINT",EDGE,{"derivedFrom":subQ0}),1.0]])]});}
            var Q2;
            {var subQ0=sQuery(id+"F0.wireOp",EDGE,"E9.13.0");Q2=makeQuery(id+"F0.imprint","IMPRINT",FACE,{"disambiguationData":[TD([[makeQuery(id+"F0.imprint","IMPRINT",EDGE,{"derivedFrom":subQ0}),1.0]])]});}
            loft(context, id + "F16", {"operationType" : NewBodyOperationType.ADD, "sheetProfilesArray" : [{ "sheetProfileEntities" : qUnion([Q1]) }, { "sheetProfileEntities" : qUnion([Q2]) }]});
        }
        {
            var Q1;
            {var subQ0=sQuery(id+"F2.wireOp",EDGE,"E19.13.0");Q1=makeQuery(id+"F2.imprint","IMPRINT",FACE,{"disambiguationData":[TD([[makeQuery(id+"F2.imprint","IMPRINT",EDGE,{"derivedFrom":subQ0}),1.0]])]});}
            var Q2;
            {var subQ0=sQuery(id+"F0.wireOp",EDGE,"E9.14.0");Q2=makeQuery(id+"F0.imprint","IMPRINT",FACE,{"disambiguationData":[TD([[makeQuery(id+"F0.imprint","IMPRINT",EDGE,{"derivedFrom":subQ0}),1.0]])]});}
            loft(context, id + "F17", {"operationType" : NewBodyOperationType.ADD, "sheetProfilesArray" : [{ "sheetProfileEntities" : qUnion([Q1]) }, { "sheetProfileEntities" : qUnion([Q2]) }]});
        }
        {
            var Q1;
            {var subQ0=sQuery(id+"F2.wireOp",EDGE,"E19.14.0");Q1=makeQuery(id+"F2.imprint","IMPRINT",FACE,{"disambiguationData":[TD([[makeQuery(id+"F2.imprint","IMPRINT",EDGE,{"derivedFrom":subQ0}),1.0]])]});}
            var Q2;
            {var subQ0=sQuery(id+"F0.wireOp",EDGE,"E9.15.0");Q2=makeQuery(id+"F0.imprint","IMPRINT",FACE,{"disambiguationData":[TD([[makeQuery(id+"F0.imprint","IMPRINT",EDGE,{"derivedFrom":subQ0}),1.0]])]});}
            loft(context, id + "F18", {"operationType" : NewBodyOperationType.ADD, "sheetProfilesArray" : [{ "sheetProfileEntities" : qUnion([Q1]) }, { "sheetProfileEntities" : qUnion([Q2]) }]});
        }
        {
            var Q1;
            {var subQ0=sQuery(id+"F2.wireOp",EDGE,"E19.15.0");Q1=makeQuery(id+"F2.imprint","IMPRINT",FACE,{"disambiguationData":[TD([[makeQuery(id+"F2.imprint","IMPRINT",EDGE,{"derivedFrom":subQ0}),1.0]])]});}
            var Q2;
            Q2=makeQuery(id+"F0.imprint","IMPRINT",FACE,{"disambiguationData":[TD([[makeQuery(id+"F0.imprint","IMPRINT",EDGE,{"derivedFrom":sQuery(id+"F0.wireOp",EDGE,"E1.trimOffspring")}),1.0]])]});
            loft(context, id + "F19", {"operationType" : NewBodyOperationType.ADD, "sheetProfilesArray" : [{ "sheetProfileEntities" : qUnion([Q1]) }, { "sheetProfileEntities" : qUnion([Q2]) }]});
        }
        {
            var Q0;
            {var subQ0=sQuery(id+"F2.wireOp",EDGE,"E10");var subQ18=makeQuery(id+"F2.imprint","INTERSECT",VERTEX,{"derivedFrom":[subQ0,sQuery(id+"F2.wireOp",EDGE,"E19.12.0")]});Q0=makeQuery(id+"F2.imprint","IMPRINT",FACE,{"disambiguationData":[TD([[makeQuery(id+"F2.imprint","IMPRINT",EDGE,{"disambiguationData":[TD([[subQ18,-1.0]])],"derivedFrom":subQ0}),1.0]])]});}
            var sketch = newSketch(context, id + "F20", { "sketchPlane" : qUnion([Q0])});
            skCircle(sketch, "E20", {"center": v(0, 0) * mm, "radius": 6.35 * mm});
            skSolve(sketch);
        }
        {
            var Q0;
            Q0 = qSketchRegion(id + "F20", true);
            extrude(context, id + "F21", {"entities" : qUnion([Q0]), "operationType" : NewBodyOperationType.REMOVE, "oppositeDirection" : true, "depth" : 50.8 * mm});
        }
    });
